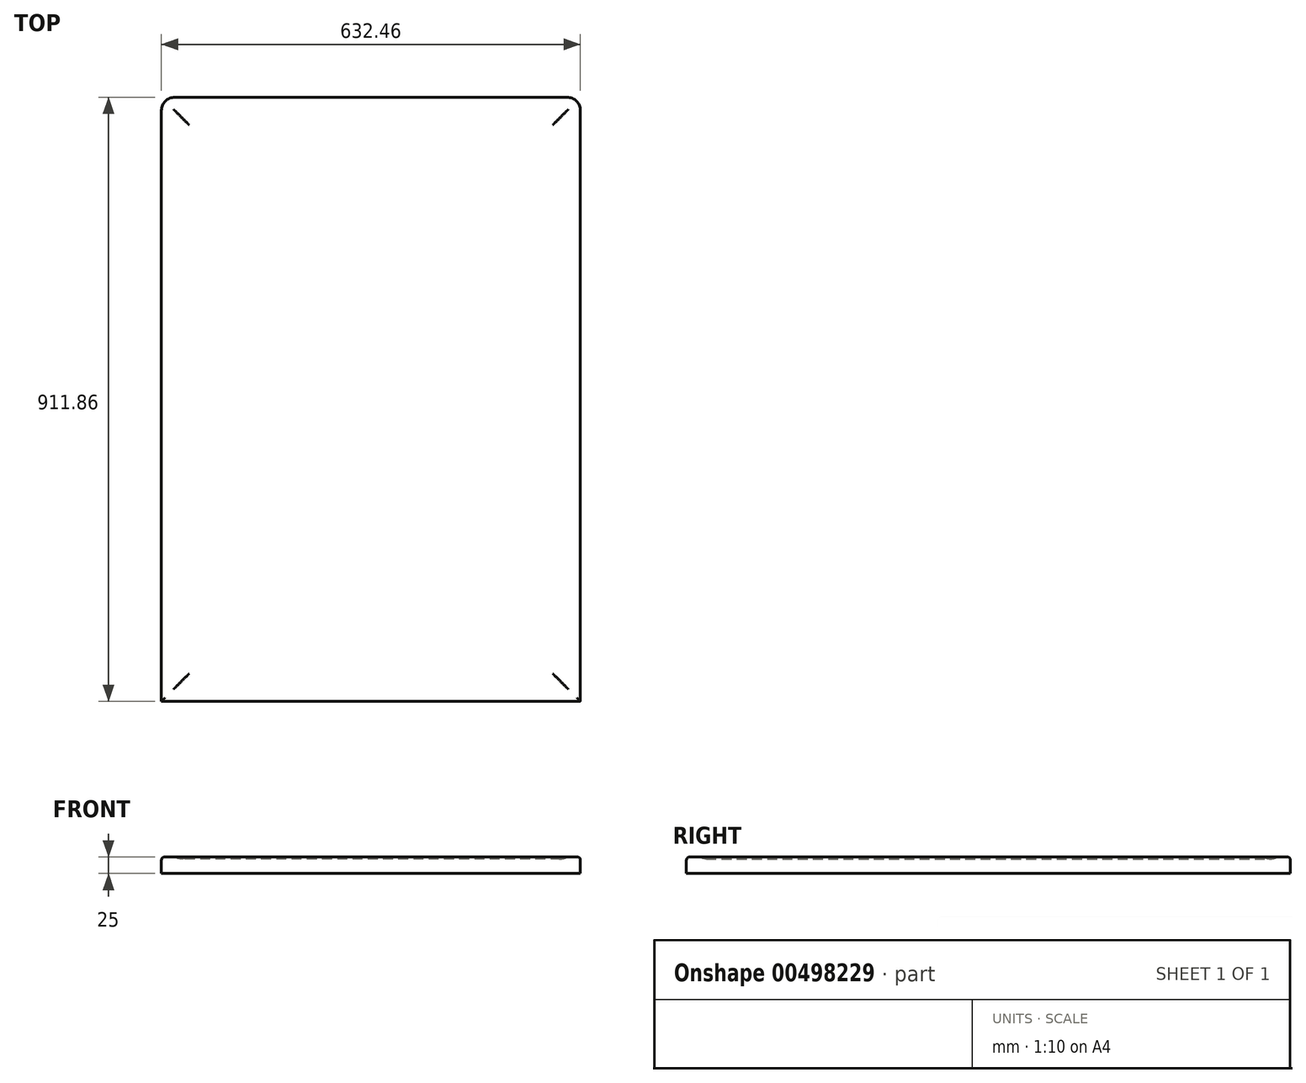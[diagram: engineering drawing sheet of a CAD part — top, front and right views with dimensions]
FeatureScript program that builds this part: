
annotation { "Feature Type Name" : "Feature", "Feature Type Description" : "" }
export const myFeature = defineFeature(function(context is Context, id is Id, definition is map)
    precondition{}
    {
        {
            var Q0;
            Q0=qCreatedBy(makeId("Top.planeOp"),FACE);
            var sketch = newSketch(context, id + "F0", { "sketchPlane" : qUnion([Q0])});
            skLineSegment(sketch, "E0.bottom", {"start": v(-316.23, 455.93) * mm, "end": v(316.23, 455.93) * mm});
            skLineSegment(sketch, "E0.top", {"start": v(-316.23, -455.93) * mm, "end": v(316.23, -455.93) * mm});
            skLineSegment(sketch, "E0.left", {"start": v(-316.23, 455.93) * mm, "end": v(-316.23, -455.93) * mm});
            skLineSegment(sketch, "E0.right", {"start": v(316.23, 455.93) * mm, "end": v(316.23, -455.93) * mm});
            skPoint(sketch, "E1", {"position": v(-316.23, 0) * mm});
            skPoint(sketch, "E2", {"position": v(0, 455.93) * mm});
            skSolve(sketch);
        }
        {
            var Q0;
            Q0=makeQuery(id+"F0.imprint","IMPRINT",FACE,{"disambiguationData":[TD([[makeQuery(id+"F0.imprint","IMPRINT",EDGE,{"derivedFrom":sQuery(id+"F0.wireOp",EDGE,"E0.bottom")}),-1.0]])]});
            extrude(context, id + "F1", {"entities" : qUnion([Q0]), "oppositeDirection" : true, "depth" : 25 * mm});
        }
        {
            var Q0;
            Q0=qCreatedBy(makeId("Top.planeOp"),FACE);
            var sketch = newSketch(context, id + "F2", { "sketchPlane" : qUnion([Q0])});
            skLineSegment(sketch, "E3.bottom", {"start": v(-286.22, 425.92) * mm, "end": v(286.22, 425.92) * mm});
            skLineSegment(sketch, "E3.top", {"start": v(-286.22, -425.92) * mm, "end": v(286.22, -425.92) * mm});
            skLineSegment(sketch, "E3.left", {"start": v(-286.22, 425.92) * mm, "end": v(-286.22, -425.92) * mm});
            skLineSegment(sketch, "E3.right", {"start": v(286.22, 425.92) * mm, "end": v(286.22, -425.92) * mm});
            skPoint(sketch, "E4", {"position": v(-286.22, 0) * mm});
            skPoint(sketch, "E5", {"position": v(0, -425.92) * mm});
            skSolve(sketch);
        }
        {
            var Q0;
            Q0=qCreatedBy(makeId("Front.planeOp"),FACE);
            var sketch = newSketch(context, id + "F3", { "sketchPlane" : qUnion([Q0])});
            skCircle(sketch, "E6", {"center": v(286.22, 15.17) * mm, "radius": 18.17 * mm});
            skLineSegment(sketch, "E7", {"start": v(276.22, 0) * mm, "end": v(296.22, 0) * mm, "construction": true});
            skLineSegment(sketch, "E8", {"start": v(286.22, 15.17) * mm, "end": v(286.22, -3) * mm, "construction": true});
            skSolve(sketch);
        }
        {
            var Q0;
            Q0 = qSketchRegion(id + "F3", true);
            var Q1;
            Q1 = qConstructionFilter(qBodyType(qCreatedBy(id + "F2" ,EDGE), BodyType.WIRE), ConstructionObject.NO);
            sweep(context, id + "F4", {"profiles" : qUnion([Q0]), "path" : qUnion([Q1])});
        }
        {
            var Q0;
            Q0=makeQuery(id+"F4.opSweep","SWEPT_BODY",BODY,{"disambiguationData":[OSD([sQuery(id+"F2.wireOp",EDGE,"E3.right"),sQuery(id+"F3.wireOp",EDGE,"E6")])]});
            var Q1;
            Q1=makeQuery(id+"F1.opExtrude","SWEPT_BODY",BODY,{"disambiguationData":[OSD([sQuery(id+"F0.wireOp",EDGE,"E0.bottom"),sQuery(id+"F0.wireOp",EDGE,"E0.top"),sQuery(id+"F0.wireOp",EDGE,"E0.left"),sQuery(id+"F0.wireOp",EDGE,"E0.right")])]});
            booleanBodies(context, id + "F5", {"operationType" : BooleanOperationType.SUBTRACTION, "tools" : qUnion([Q0]), "targets" : qUnion([Q1])});
        }
        {
            var Q0;
            Q0=makeQuery(id+"F1.opExtrude","SWEPT_EDGE",EDGE,{"disambiguationData":[OSD([sQuery(id+"F0.wireOp",EDGE,"E0.bottom"),sQuery(id+"F0.wireOp",EDGE,"E0.right")])]});
            var Q1;
            Q1=makeQuery(id+"F1.opExtrude","SWEPT_EDGE",EDGE,{"disambiguationData":[OSD([sQuery(id+"F0.wireOp",EDGE,"E0.bottom"),sQuery(id+"F0.wireOp",EDGE,"E0.left")])]});
            fillet(context, id + "F6", {"entities" : qUnion([Q0, Q1]), "radius" : 20 * mm, "tangentPropagation" : true, "allowEdgeOverflow" : false});
        }
        {
            var Q0;
            Q0=makeQuery(id+"F5.opBoolean","INTERSECT",EDGE,{"disambiguationData":[OD(0.0)],"derivedFrom":[makeQuery(id+"F1.opExtrude","CAP_FACE",FACE,{"disambiguationData":[OSD([sQuery(id+"F0.wireOp",EDGE,"E0.bottom"),sQuery(id+"F0.wireOp",EDGE,"E0.top"),sQuery(id+"F0.wireOp",EDGE,"E0.left"),sQuery(id+"F0.wireOp",EDGE,"E0.right")])],"isStart":true}),makeQuery(id+"F4.opSweep","SWEPT_FACE",FACE,{"disambiguationData":[OSD([sQuery(id+"F2.wireOp",EDGE,"E3.bottom"),sQuery(id+"F3.wireOp",EDGE,"E6")])]})]});
            var Q1;
            Q1=makeQuery(id+"F5.opBoolean","INTERSECT",EDGE,{"disambiguationData":[OD(1.0)],"derivedFrom":[makeQuery(id+"F1.opExtrude","CAP_FACE",FACE,{"disambiguationData":[OSD([sQuery(id+"F0.wireOp",EDGE,"E0.bottom"),sQuery(id+"F0.wireOp",EDGE,"E0.top"),sQuery(id+"F0.wireOp",EDGE,"E0.left"),sQuery(id+"F0.wireOp",EDGE,"E0.right")])],"isStart":true}),makeQuery(id+"F4.opSweep","SWEPT_FACE",FACE,{"disambiguationData":[OSD([sQuery(id+"F2.wireOp",EDGE,"E3.bottom"),sQuery(id+"F3.wireOp",EDGE,"E6")])]})]});
            var Q2;
            Q2=makeQuery(id+"F5.opBoolean","INTERSECT",EDGE,{"disambiguationData":[OD(0.0)],"derivedFrom":[makeQuery(id+"F1.opExtrude","CAP_FACE",FACE,{"disambiguationData":[OSD([sQuery(id+"F0.wireOp",EDGE,"E0.bottom"),sQuery(id+"F0.wireOp",EDGE,"E0.top"),sQuery(id+"F0.wireOp",EDGE,"E0.left"),sQuery(id+"F0.wireOp",EDGE,"E0.right")])],"isStart":true}),makeQuery(id+"F4.opSweep","SWEPT_FACE",FACE,{"disambiguationData":[OSD([sQuery(id+"F2.wireOp",EDGE,"E3.left"),sQuery(id+"F3.wireOp",EDGE,"E6")])]})]});
            var Q3;
            Q3=makeQuery(id+"F5.opBoolean","INTERSECT",EDGE,{"disambiguationData":[OD(1.0)],"derivedFrom":[makeQuery(id+"F1.opExtrude","CAP_FACE",FACE,{"disambiguationData":[OSD([sQuery(id+"F0.wireOp",EDGE,"E0.bottom"),sQuery(id+"F0.wireOp",EDGE,"E0.top"),sQuery(id+"F0.wireOp",EDGE,"E0.left"),sQuery(id+"F0.wireOp",EDGE,"E0.right")])],"isStart":true}),makeQuery(id+"F4.opSweep","SWEPT_FACE",FACE,{"disambiguationData":[OSD([sQuery(id+"F2.wireOp",EDGE,"E3.left"),sQuery(id+"F3.wireOp",EDGE,"E6")])]})]});
            var Q4;
            Q4=makeQuery(id+"F1.opExtrude","CAP_EDGE",EDGE,{"disambiguationData":[OSD([sQuery(id+"F0.wireOp",EDGE,"E0.bottom")])],"isStart":true});
            var Q5;
            {var subQ0=sQuery(id+"F0.wireOp",EDGE,"E0.left");var subQ1=sQuery(id+"F0.wireOp",EDGE,"E0.top");var subQ2=sQuery(id+"F0.wireOp",EDGE,"E0.right");var subQ3=sQuery(id+"F0.wireOp",EDGE,"E0.bottom");var subQ4=sQuery(id+"F3.wireOp",EDGE,"E6");Q5=makeQuery(id+"F6.opFillet","BLEND_EDGE",EDGE,{"blendedFrom":[makeQuery(id+"F1.opExtrude","SWEPT_EDGE",EDGE,{"disambiguationData":[OSD([subQ3,subQ0])]}),makeQuery(id+"F5.opBoolean","SPLIT",FACE,{"disambiguationData":[TD([makeQuery(id+"F1.opExtrude","SWEPT_FACE",FACE,{"disambiguationData":[OSD([subQ3])]}),makeQuery(id+"F1.opExtrude","SWEPT_FACE",FACE,{"disambiguationData":[OSD([subQ1])]}),makeQuery(id+"F1.opExtrude","SWEPT_FACE",FACE,{"disambiguationData":[OSD([subQ0])]}),makeQuery(id+"F1.opExtrude","SWEPT_FACE",FACE,{"disambiguationData":[OSD([subQ2])]}),makeQuery(id+"F4.opSweep","SWEPT_FACE",FACE,{"disambiguationData":[OSD([sQuery(id+"F2.wireOp",EDGE,"E3.bottom"),subQ4])]}),makeQuery(id+"F4.opSweep","SWEPT_FACE",FACE,{"disambiguationData":[OSD([sQuery(id+"F2.wireOp",EDGE,"E3.top"),subQ4])]}),makeQuery(id+"F4.opSweep","SWEPT_FACE",FACE,{"disambiguationData":[OSD([sQuery(id+"F2.wireOp",EDGE,"E3.left"),subQ4])]}),makeQuery(id+"F4.opSweep","SWEPT_FACE",FACE,{"disambiguationData":[OSD([sQuery(id+"F2.wireOp",EDGE,"E3.right"),subQ4])]})])],"derivedFrom":makeQuery(id+"F1.opExtrude","CAP_FACE",FACE,{"disambiguationData":[OSD([subQ3,subQ1,subQ0,subQ2])],"isStart":true})})],"blendedInto":[makeQuery(id+"F5.opBoolean","SPLIT",FACE,{"disambiguationData":[TD([makeQuery(id+"F1.opExtrude","SWEPT_FACE",FACE,{"disambiguationData":[OSD([subQ3])]}),makeQuery(id+"F1.opExtrude","SWEPT_FACE",FACE,{"disambiguationData":[OSD([subQ1])]}),makeQuery(id+"F1.opExtrude","SWEPT_FACE",FACE,{"disambiguationData":[OSD([subQ0])]}),makeQuery(id+"F1.opExtrude","SWEPT_FACE",FACE,{"disambiguationData":[OSD([subQ2])]}),makeQuery(id+"F4.opSweep","SWEPT_FACE",FACE,{"disambiguationData":[OSD([sQuery(id+"F2.wireOp",EDGE,"E3.bottom"),subQ4])]}),makeQuery(id+"F4.opSweep","SWEPT_FACE",FACE,{"disambiguationData":[OSD([sQuery(id+"F2.wireOp",EDGE,"E3.top"),subQ4])]}),makeQuery(id+"F4.opSweep","SWEPT_FACE",FACE,{"disambiguationData":[OSD([sQuery(id+"F2.wireOp",EDGE,"E3.left"),subQ4])]}),makeQuery(id+"F4.opSweep","SWEPT_FACE",FACE,{"disambiguationData":[OSD([sQuery(id+"F2.wireOp",EDGE,"E3.right"),subQ4])]})])],"derivedFrom":makeQuery(id+"F1.opExtrude","CAP_FACE",FACE,{"disambiguationData":[OSD([subQ3,subQ1,subQ0,subQ2])],"isStart":true})})]});}
            var Q6;
            Q6=makeQuery(id+"F1.opExtrude","CAP_EDGE",EDGE,{"disambiguationData":[OSD([sQuery(id+"F0.wireOp",EDGE,"E0.left")])],"isStart":true});
            var Q7;
            {var subQ0=sQuery(id+"F0.wireOp",EDGE,"E0.left");var subQ1=sQuery(id+"F0.wireOp",EDGE,"E0.top");var subQ2=sQuery(id+"F0.wireOp",EDGE,"E0.right");var subQ3=sQuery(id+"F0.wireOp",EDGE,"E0.bottom");var subQ4=sQuery(id+"F3.wireOp",EDGE,"E6");Q7=makeQuery(id+"F6.opFillet","BLEND_EDGE",EDGE,{"blendedFrom":[makeQuery(id+"F1.opExtrude","SWEPT_EDGE",EDGE,{"disambiguationData":[OSD([subQ3,subQ2])]}),makeQuery(id+"F5.opBoolean","SPLIT",FACE,{"disambiguationData":[TD([makeQuery(id+"F1.opExtrude","SWEPT_FACE",FACE,{"disambiguationData":[OSD([subQ3])]}),makeQuery(id+"F1.opExtrude","SWEPT_FACE",FACE,{"disambiguationData":[OSD([subQ1])]}),makeQuery(id+"F1.opExtrude","SWEPT_FACE",FACE,{"disambiguationData":[OSD([subQ0])]}),makeQuery(id+"F1.opExtrude","SWEPT_FACE",FACE,{"disambiguationData":[OSD([subQ2])]}),makeQuery(id+"F4.opSweep","SWEPT_FACE",FACE,{"disambiguationData":[OSD([sQuery(id+"F2.wireOp",EDGE,"E3.bottom"),subQ4])]}),makeQuery(id+"F4.opSweep","SWEPT_FACE",FACE,{"disambiguationData":[OSD([sQuery(id+"F2.wireOp",EDGE,"E3.top"),subQ4])]}),makeQuery(id+"F4.opSweep","SWEPT_FACE",FACE,{"disambiguationData":[OSD([sQuery(id+"F2.wireOp",EDGE,"E3.left"),subQ4])]}),makeQuery(id+"F4.opSweep","SWEPT_FACE",FACE,{"disambiguationData":[OSD([sQuery(id+"F2.wireOp",EDGE,"E3.right"),subQ4])]})])],"derivedFrom":makeQuery(id+"F1.opExtrude","CAP_FACE",FACE,{"disambiguationData":[OSD([subQ3,subQ1,subQ0,subQ2])],"isStart":true})})],"blendedInto":[makeQuery(id+"F5.opBoolean","SPLIT",FACE,{"disambiguationData":[TD([makeQuery(id+"F1.opExtrude","SWEPT_FACE",FACE,{"disambiguationData":[OSD([subQ3])]}),makeQuery(id+"F1.opExtrude","SWEPT_FACE",FACE,{"disambiguationData":[OSD([subQ1])]}),makeQuery(id+"F1.opExtrude","SWEPT_FACE",FACE,{"disambiguationData":[OSD([subQ0])]}),makeQuery(id+"F1.opExtrude","SWEPT_FACE",FACE,{"disambiguationData":[OSD([subQ2])]}),makeQuery(id+"F4.opSweep","SWEPT_FACE",FACE,{"disambiguationData":[OSD([sQuery(id+"F2.wireOp",EDGE,"E3.bottom"),subQ4])]}),makeQuery(id+"F4.opSweep","SWEPT_FACE",FACE,{"disambiguationData":[OSD([sQuery(id+"F2.wireOp",EDGE,"E3.top"),subQ4])]}),makeQuery(id+"F4.opSweep","SWEPT_FACE",FACE,{"disambiguationData":[OSD([sQuery(id+"F2.wireOp",EDGE,"E3.left"),subQ4])]}),makeQuery(id+"F4.opSweep","SWEPT_FACE",FACE,{"disambiguationData":[OSD([sQuery(id+"F2.wireOp",EDGE,"E3.right"),subQ4])]})])],"derivedFrom":makeQuery(id+"F1.opExtrude","CAP_FACE",FACE,{"disambiguationData":[OSD([subQ3,subQ1,subQ0,subQ2])],"isStart":true})})]});}
            var Q8;
            Q8=makeQuery(id+"F5.opBoolean","INTERSECT",EDGE,{"disambiguationData":[OD(1.0)],"derivedFrom":[makeQuery(id+"F1.opExtrude","CAP_FACE",FACE,{"disambiguationData":[OSD([sQuery(id+"F0.wireOp",EDGE,"E0.bottom"),sQuery(id+"F0.wireOp",EDGE,"E0.top"),sQuery(id+"F0.wireOp",EDGE,"E0.left"),sQuery(id+"F0.wireOp",EDGE,"E0.right")])],"isStart":true}),makeQuery(id+"F4.opSweep","SWEPT_FACE",FACE,{"disambiguationData":[OSD([sQuery(id+"F2.wireOp",EDGE,"E3.right"),sQuery(id+"F3.wireOp",EDGE,"E6")])]})]});
            var Q9;
            Q9=makeQuery(id+"F5.opBoolean","INTERSECT",EDGE,{"disambiguationData":[OD(0.0)],"derivedFrom":[makeQuery(id+"F1.opExtrude","CAP_FACE",FACE,{"disambiguationData":[OSD([sQuery(id+"F0.wireOp",EDGE,"E0.bottom"),sQuery(id+"F0.wireOp",EDGE,"E0.top"),sQuery(id+"F0.wireOp",EDGE,"E0.left"),sQuery(id+"F0.wireOp",EDGE,"E0.right")])],"isStart":true}),makeQuery(id+"F4.opSweep","SWEPT_FACE",FACE,{"disambiguationData":[OSD([sQuery(id+"F2.wireOp",EDGE,"E3.right"),sQuery(id+"F3.wireOp",EDGE,"E6")])]})]});
            var Q10;
            Q10=makeQuery(id+"F1.opExtrude","CAP_EDGE",EDGE,{"disambiguationData":[OSD([sQuery(id+"F0.wireOp",EDGE,"E0.right")])],"isStart":true});
            var Q11;
            Q11=makeQuery(id+"F5.opBoolean","INTERSECT",EDGE,{"disambiguationData":[OD(0.0)],"derivedFrom":[makeQuery(id+"F1.opExtrude","CAP_FACE",FACE,{"disambiguationData":[OSD([sQuery(id+"F0.wireOp",EDGE,"E0.bottom"),sQuery(id+"F0.wireOp",EDGE,"E0.top"),sQuery(id+"F0.wireOp",EDGE,"E0.left"),sQuery(id+"F0.wireOp",EDGE,"E0.right")])],"isStart":true}),makeQuery(id+"F4.opSweep","SWEPT_FACE",FACE,{"disambiguationData":[OSD([sQuery(id+"F2.wireOp",EDGE,"E3.top"),sQuery(id+"F3.wireOp",EDGE,"E6")])]})]});
            var Q12;
            Q12=makeQuery(id+"F5.opBoolean","INTERSECT",EDGE,{"disambiguationData":[OD(1.0)],"derivedFrom":[makeQuery(id+"F1.opExtrude","CAP_FACE",FACE,{"disambiguationData":[OSD([sQuery(id+"F0.wireOp",EDGE,"E0.bottom"),sQuery(id+"F0.wireOp",EDGE,"E0.top"),sQuery(id+"F0.wireOp",EDGE,"E0.left"),sQuery(id+"F0.wireOp",EDGE,"E0.right")])],"isStart":true}),makeQuery(id+"F4.opSweep","SWEPT_FACE",FACE,{"disambiguationData":[OSD([sQuery(id+"F2.wireOp",EDGE,"E3.top"),sQuery(id+"F3.wireOp",EDGE,"E6")])]})]});
            var Q13;
            Q13=makeQuery(id+"F1.opExtrude","CAP_EDGE",EDGE,{"disambiguationData":[OSD([sQuery(id+"F0.wireOp",EDGE,"E0.top")])],"isStart":true});
            fillet(context, id + "F7", {"entities" : qUnion([Q0, Q1, Q2, Q3, Q4, Q5, Q6, Q7, Q8, Q9, Q10, Q11, Q12, Q13]), "radius" : 5 * mm, "tangentPropagation" : true, "allowEdgeOverflow" : false});
        }
    });
